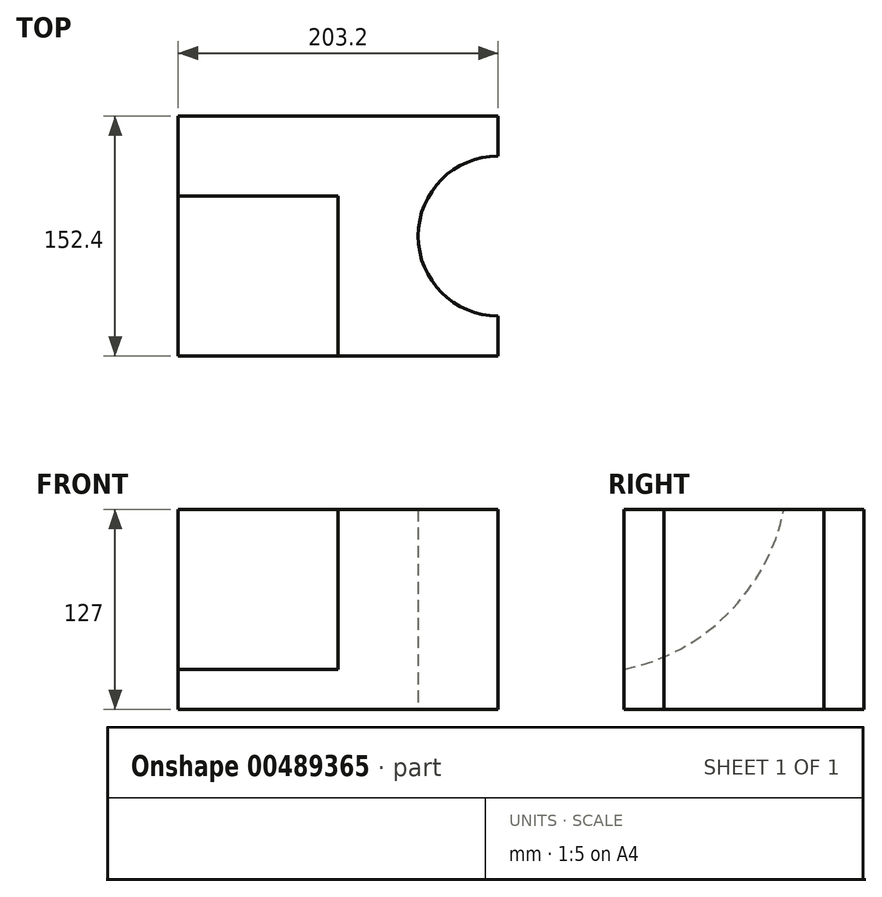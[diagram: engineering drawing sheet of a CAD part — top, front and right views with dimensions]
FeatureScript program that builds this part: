
annotation { "Feature Type Name" : "Feature", "Feature Type Description" : "" }
export const myFeature = defineFeature(function(context is Context, id is Id, definition is map)
    precondition{}
    {
        {
            var Q0;
            Q0=qCreatedBy(makeId("Top.planeOp"),FACE);
            var sketch = newSketch(context, id + "F0", { "sketchPlane" : qUnion([Q0])});
            skLineSegment(sketch, "E0.bottom", {"start": v(-106.88, 76.2) * mm, "end": v(96.32, 76.2) * mm});
            skLineSegment(sketch, "E0.top", {"start": v(-106.88, -76.2) * mm, "end": v(96.32, -76.2) * mm});
            skLineSegment(sketch, "E0.left", {"start": v(-106.88, 76.2) * mm, "end": v(-106.88, -76.2) * mm});
            skLineSegment(sketch, "E0.right", {"start": v(96.32, 76.2) * mm, "end": v(96.32, -76.2) * mm});
            skPoint(sketch, "E0.middle", {"position": v(-5.28, 0) * mm});
            skPoint(sketch, "E1", {"position": v(96.32, -50.8) * mm});
            skPoint(sketch, "E2", {"position": v(96.32, 50.8) * mm});
            skArc(sketch, "E3", {"start": v(96.32, 50.8) * mm, "mid": v(45.52, 0) * mm, "end": v(96.32, -50.8) * mm});
            skSolve(sketch);
        }
        {
            var Q0;
            {var subQ1=sQuery(id+"F0.wireOp",EDGE,"E0.bottom");Q0=makeQuery(id+"F0.imprint","IMPRINT",FACE,{"disambiguationData":[TD([[makeQuery(id+"F0.imprint","IMPRINT",EDGE,{"derivedFrom":subQ1}),-1.0]])]});}
            extrude(context, id + "F1", {"entities" : qUnion([Q0]), "depth" : 127 * mm});
        }
        {
            var Q0;
            Q0=makeQuery(id+"F1.opExtrude","SWEPT_FACE",FACE,{"disambiguationData":[OSD([sQuery(id+"F0.wireOp",EDGE,"E0.left")])]});
            var sketch = newSketch(context, id + "F2", { "sketchPlane" : qUnion([Q0])});
            skArc(sketch, "E4", {"start": v(-25.4, 127) * mm, "mid": v(10.13, 60.93) * mm, "end": v(76.2, 25.4) * mm});
            skSolve(sketch);
        }
        {
            var Q0;
            Q0=qSketchRegion(id+"F2",true);
            var Q1;
            {var subQ0=sQuery(id+"F2.wireOp",EDGE,"E4");Q1=makeQuery(id+"F2.imprint","IMPRINT",FACE,{"disambiguationData":[TD([[makeQuery(id+"F2.imprint","IMPRINT",EDGE,{"derivedFrom":subQ0}),1.0]])]});}
            extrude(context, id + "F3", {"entities" : qUnion([Q0, Q1]), "operationType" : NewBodyOperationType.REMOVE, "oppositeDirection" : true, "depth" : 101.6 * mm});
        }
    });
